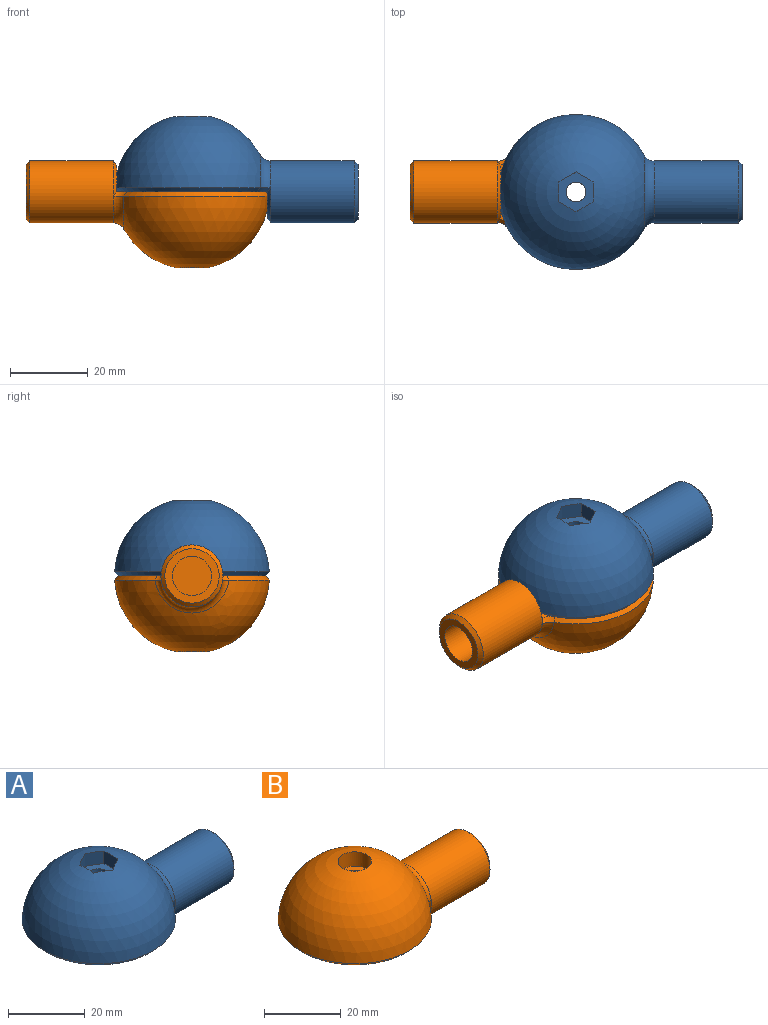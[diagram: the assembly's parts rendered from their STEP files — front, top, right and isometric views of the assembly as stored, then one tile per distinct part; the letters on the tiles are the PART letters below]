
ASSEMBLY  parts=2 mates=1
PART A: 23 faces, bbox 62.8x40x27.5 mm
  f0: cylinder r=2.55mm len=15.4mm, axis (0,0,-1), area 246.7mm2, adj f3,f22
  f1: cylinder r=8mm len=21.6mm, axis (-1,0,0), area 1082.2mm2, adj f6,f9,f10,f11,f15
  f2: sphere r=20mm, area 2179.4mm2, adj f6,f13,f16,f17,f18,f19,f20,f21
  f3: plane 39.5x37.97mm, normal (0,0,-1), area 1134.3mm2, adj f0,f5,f9,f12,f13,f14
  f4: plane 14x14mm, normal (1,0,0), area 73.8mm2, adj f7,f10
  f5: sphere r=20.5mm, area 71.9mm2, adj f3,f9
  f6: torus R=11mm, axis (-1,0,0), area 79.4mm2, adj f1,f2,f12,f14
  f7: cylinder r=5.05mm len=15mm, axis (1,0,0), area 476mm2, adj f4,f8
  f8: plane 10.1x10.1mm, normal (1,0,0), area 80.1mm2, adj f7
  f9: cone r=8mm half-angle=54.5deg, axis (1,0,0), area 39mm2, adj f1,f3,f5,f11,f12,f14,f15
  f10: cone r=7mm half-angle=45deg, axis (-1,0,0), area 66.6mm2, adj f1,f4
  f11: plane 0.19x0.16mm, normal (0,-0.76,-0.65), area 0mm2, adj f1,f9,f12
  f12: bspline ~3.51x2.58mm, area 5.2mm2, adj f3,f6,f9,f11,f13
  f13: cone r=19.97mm half-angle=43.5deg, axis (0,0,1), area 149.5mm2, adj f2,f3,f12,f14
  f14: bspline ~3.51x2.58mm, area 5.2mm2, adj f3,f6,f9,f13,f15
  f15: plane 0.19x0.16mm, normal (0,0.76,-0.65), area 0mm2, adj f1,f9,f14
  f16: plane 5.14x4.1mm, normal (-1,0,0), area 20.8mm2, adj f2,f17,f21,f22
  f17: plane 4.44x4.1mm, normal (-0.5,-0.86,0), area 20.8mm2, adj f2,f16,f18,f22
  f18: plane 4.46x4.1mm, normal (0.5,-0.87,0), area 20.8mm2, adj f2,f17,f19,f22
  f19: plane 5.14x4.1mm, normal (1,0,0), area 20.8mm2, adj f2,f18,f20,f22
  f20: plane 4.44x4.1mm, normal (0.5,0.86,0), area 20.8mm2, adj f2,f19,f21,f22
  f21: plane 4.46x4.1mm, normal (-0.5,0.87,0), area 20.8mm2, adj f2,f16,f20,f22
  f22: plane 10.28x8.91mm, normal (0,0,1), area 48.2mm2, adj f0,f16,f17,f18,f19,f20,f21
PART B: 18 faces, bbox 62.8x40x27.5 mm
  f0: cylinder r=8mm len=21.6mm, axis (-1,0,0), area 1082.2mm2, adj f5,f8,f9,f13,f17
  f1: sphere r=20mm, area 2188.8mm2, adj f5,f10,f15
  f2: plane 39.5x37.97mm, normal (0,0,-1), area 1134.3mm2, adj f4,f8,f12,f14,f15,f16
  f3: plane 14x14mm, normal (1,0,0), area 73.8mm2, adj f6,f9
  f4: sphere r=20.5mm, area 71.9mm2, adj f2,f8
  f5: torus R=11mm, axis (-1,0,0), area 79.4mm2, adj f0,f1,f14,f16
  f6: cylinder r=5.05mm len=15mm, axis (1,0,0), area 476mm2, adj f3,f7
  f7: plane 10.1x10.1mm, normal (1,0,0), area 80.1mm2, adj f6
  f8: cone r=8mm half-angle=54.5deg, axis (1,0,0), area 39mm2, adj f0,f2,f4,f13,f14,f16,f17
  f9: cone r=7mm half-angle=45deg, axis (-1,0,0), area 66.6mm2, adj f0,f3
  f10: cylinder r=4.35mm len=8.7mm, axis (0,0,1), area 123.6mm2, adj f1,f11
  f11: plane 8.7x8.7mm, normal (0,0,1), area 39mm2, adj f10,f12
  f12: cylinder r=2.55mm len=15mm, axis (0,0,-1), area 240.3mm2, adj f2,f11
  f13: plane 0.19x0.16mm, normal (0,-0.76,-0.65), area 0mm2, adj f0,f8,f14
  f14: bspline ~3.51x2.58mm, area 5.2mm2, adj f2,f5,f8,f13,f15
  f15: cone r=19.97mm half-angle=43.5deg, axis (0,0,1), area 149.5mm2, adj f1,f2,f14,f16
  f16: bspline ~3.51x2.58mm, area 5.2mm2, adj f2,f5,f8,f15,f17
  f17: plane 0.19x0.16mm, normal (0,0.76,-0.65), area 0mm2, adj f0,f8,f16
PLACE A t=(-0.78,1.02,9.71)mm
PLACE B rot(axis=(0,1,0),180deg) t=(-0.78,1.02,9.71)mm
MATE fastened B.f12 <-> A.f0  axis (0,0,1) through (-0.78,1.02,9.71)mm
